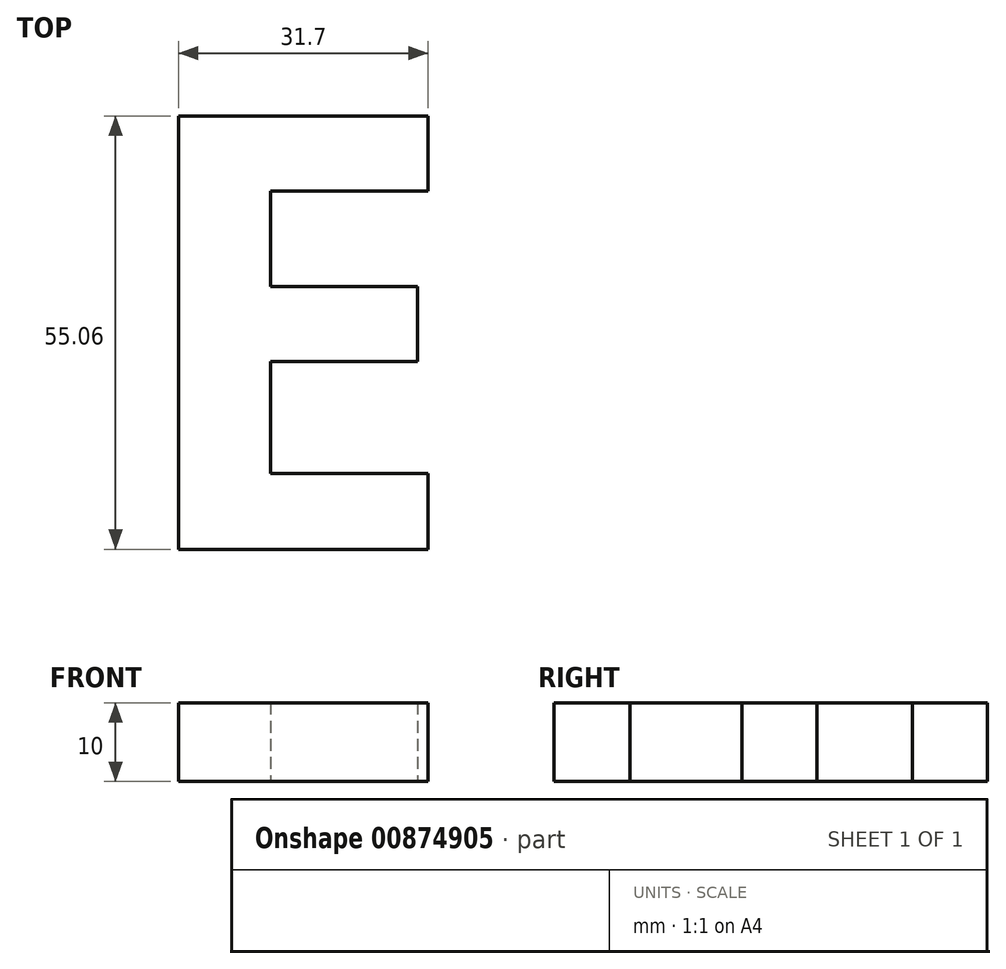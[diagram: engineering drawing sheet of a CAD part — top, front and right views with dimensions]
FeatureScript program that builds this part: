
annotation { "Feature Type Name" : "Feature", "Feature Type Description" : "" }
export const myFeature = defineFeature(function(context is Context, id is Id, definition is map)
    precondition{}
    {
        {
            var Q0;
            Q0=qCreatedBy(makeId("Top.planeOp"),FACE);
            var sketch = newSketch(context, id + "F0", { "sketchPlane" : qUnion([Q0])});
            skText(sketch, "E0", { "text": "E", "fontName": "OpenSans-Bold.ttf"});
            const initialGuessF0  = {"E0": [0, 0, 1, 0, 0.05553]};
            skSetInitialGuess(sketch, initialGuessF0);
            skSolve(sketch);
        }
        {
            var Q0;
            Q0 = qSketchRegion(id + "F0", true);
            extrude(context, id + "F1", {"entities" : qUnion([Q0]), "depth" : 10 * mm, "offsetDistance" : 25.4 * mm});
        }
    });
